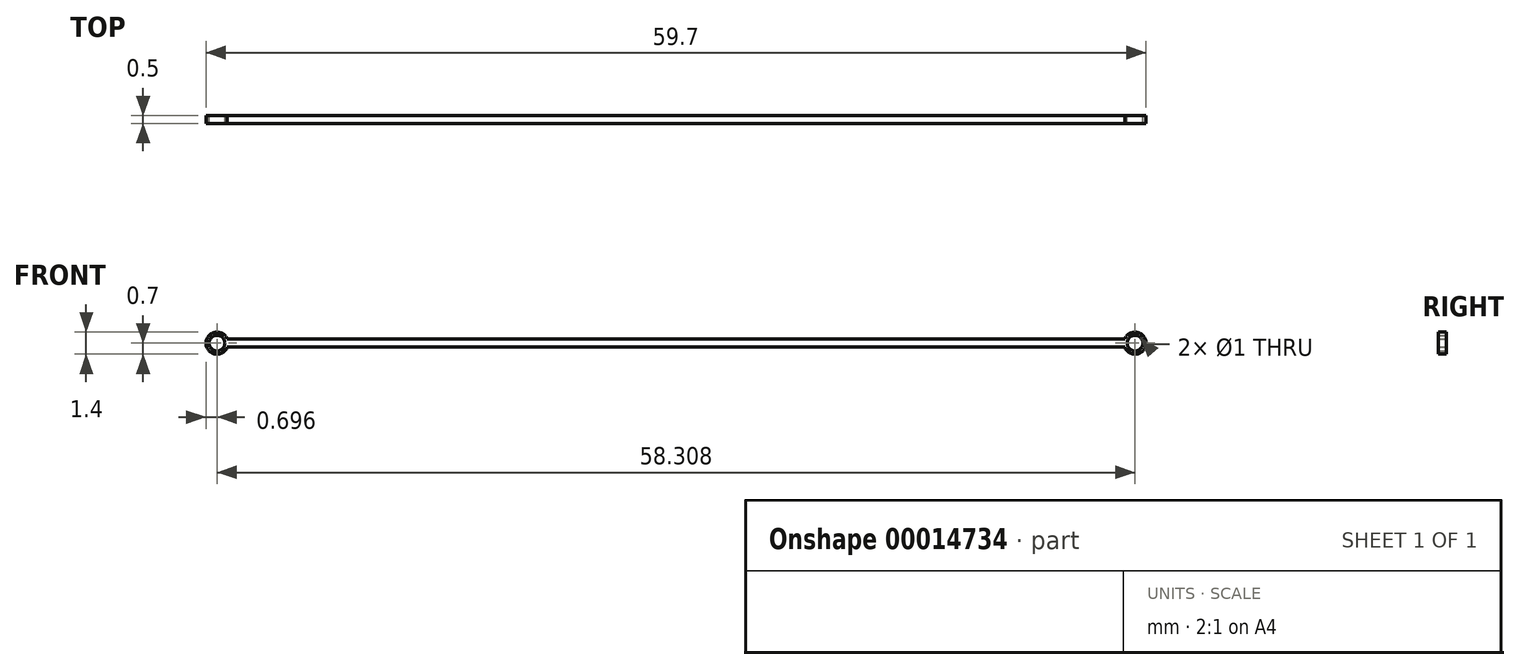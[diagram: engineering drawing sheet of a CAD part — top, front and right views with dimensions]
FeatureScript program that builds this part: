
annotation { "Feature Type Name" : "Feature", "Feature Type Description" : "" }
export const myFeature = defineFeature(function(context is Context, id is Id, definition is map)
    precondition{}
    {
        {
            var Q0;
            Q0=qCreatedBy(makeId("Front.planeOp"),FACE);
            var sketch = newSketch(context, id + "F0", { "sketchPlane" : qUnion([Q0])});
            skLineSegment(sketch, "E0.bottom", {"start": v(0, 0) * mm, "end": v(57, 0) * mm});
            skLineSegment(sketch, "E0.top", {"start": v(0, 0.5) * mm, "end": v(57, 0.5) * mm});
            skLineSegment(sketch, "E0.left", {"start": v(0, 0) * mm, "end": v(0, 0.5) * mm});
            skLineSegment(sketch, "E0.right", {"start": v(57, 0) * mm, "end": v(57, 0.5) * mm});
            skArc(sketch, "E1", {"start": v(0, 0.5) * mm, "mid": v(-1.35, 0.25) * mm, "end": v(0, 0) * mm});
            skArc(sketch, "E2", {"start": v(57, 0) * mm, "mid": v(58.35, 0.25) * mm, "end": v(57, 0.5) * mm});
            skCircle(sketch, "E3", {"center": v(-0.65, 0.25) * mm, "radius": 0.5 * mm});
            skCircle(sketch, "E4", {"center": v(57.65, 0.25) * mm, "radius": 0.5 * mm});
            skSolve(sketch);
        }
        {
            var Q0;
            Q0=qSketchRegion(id+"F0",true);
            extrude(context, id + "F1", {"entities" : qUnion([Q0]), "depth" : 0.5 * mm});
        }
    });
